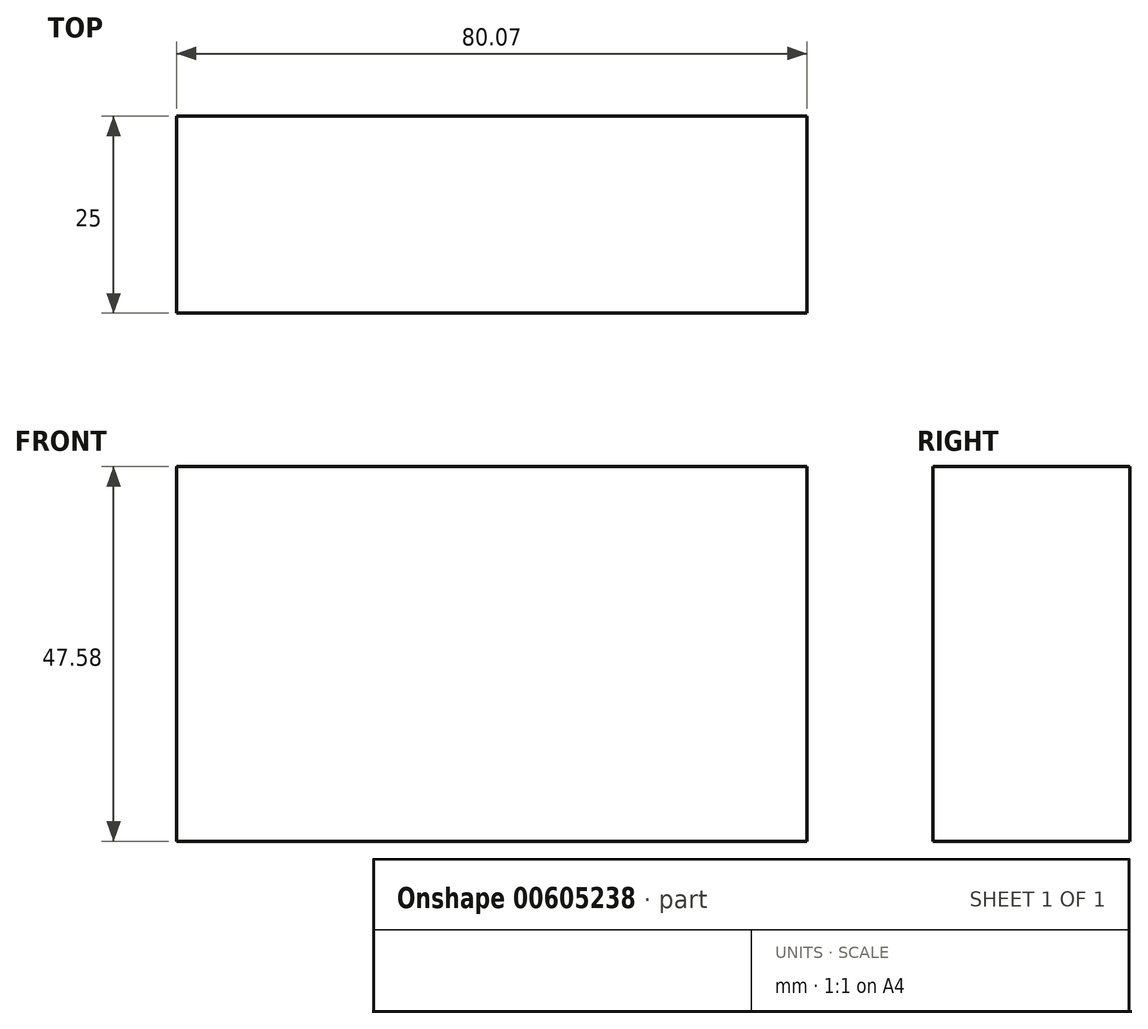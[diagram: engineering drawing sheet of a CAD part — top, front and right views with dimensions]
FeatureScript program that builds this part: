
annotation { "Feature Type Name" : "Feature", "Feature Type Description" : "" }
export const myFeature = defineFeature(function(context is Context, id is Id, definition is map)
    precondition{}
    {
        {
            var Q0;
            Q0=qCreatedBy(makeId("Front.planeOp"),FACE);
            var sketch = newSketch(context, id + "F0", { "sketchPlane" : qUnion([Q0])});
            skLineSegment(sketch, "E0.bottom", {"start": v(-32.64, 14.02) * mm, "end": v(47.43, 14.02) * mm});
            skLineSegment(sketch, "E0.top", {"start": v(-32.64, -33.56) * mm, "end": v(47.43, -33.56) * mm});
            skLineSegment(sketch, "E0.left", {"start": v(-32.64, 14.02) * mm, "end": v(-32.64, -33.56) * mm});
            skLineSegment(sketch, "E0.right", {"start": v(47.43, 14.02) * mm, "end": v(47.43, -33.56) * mm});
            skSolve(sketch);
        }
        {
            var Q0;
            Q0 = qSketchRegion(id + "F0", true);
            extrude(context, id + "F1", {"entities" : qUnion([Q0]), "depth" : 25 * mm, "offsetDistance" : 25 * mm});
        }
    });
